# Revit family: Detail-Shades-Hunter_Douglas-RB500-Standard_Duty-Clutch-Bracket-38-Pocket_Details
name_source: partatom
category: Detail Items
units: mm (PartAtom-declared; Revit-internal decimal feet)

## family parameters
OmniClass Number = 23.30.60.14
OmniClass Title = Interior Window Treatment
Rotate with component = No
Section Shape = Not Defined
Shared = No

## types (3) — shared parameters
Assembly Code = E2010300
CD_Install Documentation = https://www.hunterdouglasarchitectural.com
CD_Microsite = https://microsite.caddetails.com
CD_Product Documentation Link = https://www.hunterdouglasarchitectural.com
CD_Product Name = RB 500 Roller Shade System
CD_Product Page URL = https://www.hunterdouglasarchitectural.com
CD_Warranty = https://assets.hunterdouglasarchitectural.com
Description = Standard Duty Roller Shade
Manufacturer = Hunter Douglas Architectural
Model = Standard Clutch 38 Bracket
URL = https://www.hunterdouglasarchitectural.com

## per-type parameters (varying)
| type | CD_Gypsum Pocket | CD_Height | CD_Not Gypsum | CD_Surface Pocket | CD_Tile Pocket | CD_Width |
| Surface Pocket | No | 5 9/32" | Yes | Yes | No | 5 9/32" |
| Tile Pocket | No | 5 9/32" | Yes | No | Yes | 5 9/32" |
| Gypsum Pocket | Yes | 5" | No | No | No | 5" |

note: column(s) folded — value = type name in every type: Type Comments

## geometry (parser evidence)
native form markers: Sweep x2
no freeform markers — native parametric forms only
